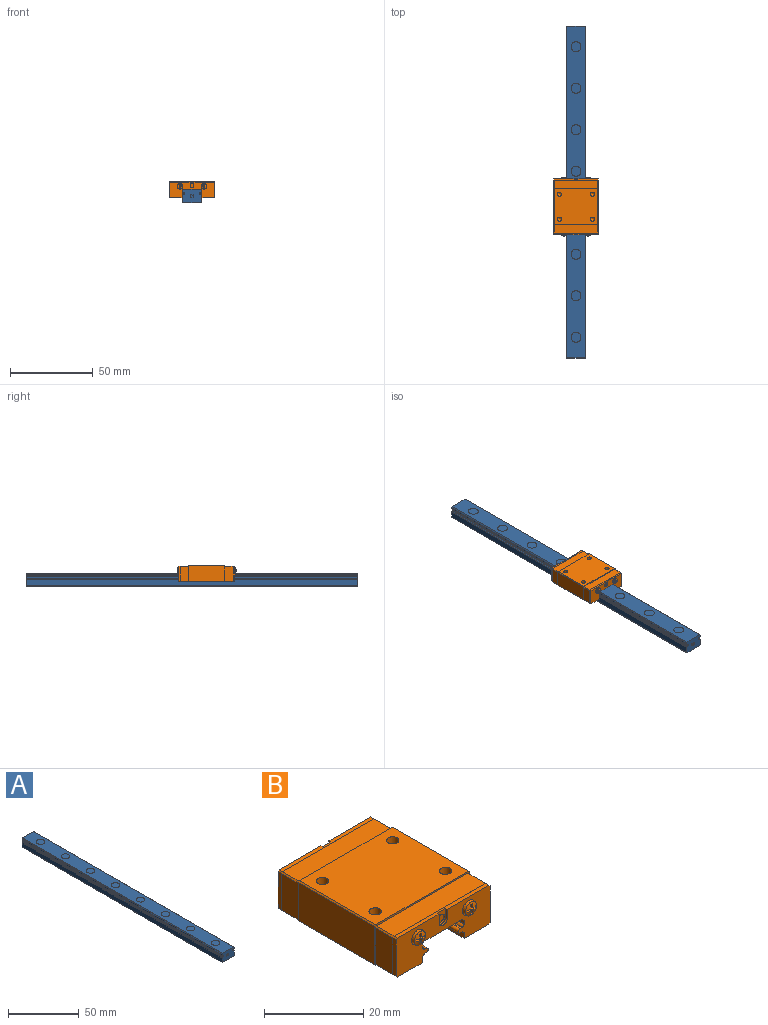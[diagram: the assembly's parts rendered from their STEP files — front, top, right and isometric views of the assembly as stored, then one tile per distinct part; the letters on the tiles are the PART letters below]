
ASSEMBLY  parts=2 mates=1
PART A: 141 faces, bbox 12x200x8 mm
  f0: cylinder r=0.5mm len=200mm, axis (0,1,0), area 377.3mm2, adj f82,f106,f134,f135
  f1: cylinder r=0.5mm len=200mm, axis (0,1,0), area 377.3mm2, adj f82,f106,f121,f122
  f2: cylinder r=1.75mm len=3.5mm, axis (0,0,-1), area 38.5mm2, adj f114,f115
  f3: cylinder r=3mm len=6mm, axis (0,0,-1), area 0.2mm2, adj f40,f128
  f4: cylinder r=1.75mm len=3.5mm, axis (0,0,-1), area 38.5mm2, adj f113,f115
  f5: cylinder r=3mm len=6mm, axis (0,0,-1), area 0.2mm2, adj f38,f128
  f6: cylinder r=1.75mm len=3.5mm, axis (0,0,-1), area 38.5mm2, adj f112,f115
  f7: cylinder r=3mm len=6mm, axis (0,0,-1), area 0.2mm2, adj f36,f128
  f8: cylinder r=1.75mm len=3.5mm, axis (0,0,-1), area 38.5mm2, adj f111,f115
  f9: cylinder r=3mm len=6mm, axis (0,0,-1), area 0.2mm2, adj f34,f128
  f10: cylinder r=1.75mm len=3.5mm, axis (0,0,-1), area 38.5mm2, adj f110,f115
  f11: cylinder r=3mm len=6mm, axis (0,0,-1), area 0.2mm2, adj f32,f128
  f12: cylinder r=1.75mm len=3.5mm, axis (0,0,-1), area 38.5mm2, adj f109,f115
  f13: cylinder r=3mm len=6mm, axis (0,0,-1), area 0.2mm2, adj f30,f128
  f14: cylinder r=1.75mm len=3.5mm, axis (0,0,-1), area 38.5mm2, adj f108,f115
  f15: cylinder r=3mm len=6mm, axis (0,0,-1), area 0.2mm2, adj f28,f128
  f16: cylinder r=1.75mm len=3.5mm, axis (0,0,-1), area 38.5mm2, adj f107,f115
  f17: cylinder r=3mm len=6mm, axis (0,0,-1), area 0.2mm2, adj f26,f128
  f18: cylinder r=3mm len=6mm, axis (0,0,-1), area 75.2mm2, adj f41,f114
  f19: cylinder r=3mm len=6mm, axis (0,0,-1), area 75.2mm2, adj f39,f113
  f20: cylinder r=3mm len=6mm, axis (0,0,-1), area 75.2mm2, adj f37,f112
  f21: cylinder r=3mm len=6mm, axis (0,0,-1), area 75.2mm2, adj f35,f111
  f22: cylinder r=3mm len=6mm, axis (0,0,-1), area 75.2mm2, adj f33,f110
  f23: cylinder r=3mm len=6mm, axis (0,0,-1), area 75.2mm2, adj f31,f109
  f24: cylinder r=3mm len=6mm, axis (0,0,-1), area 75.2mm2, adj f29,f108
  f25: cylinder r=3mm len=6mm, axis (0,0,-1), area 75.2mm2, adj f27,f107
  f26: plane 6x6mm, normal (0,0,1), area 28.3mm2, adj f17
  f27: plane 6x6mm, normal (0,0,-1), area 28.3mm2, adj f25
  f28: plane 6x6mm, normal (0,0,1), area 28.3mm2, adj f15
  f29: plane 6x6mm, normal (0,0,-1), area 28.3mm2, adj f24
  f30: plane 6x6mm, normal (0,0,1), area 28.3mm2, adj f13
  f31: plane 6x6mm, normal (0,0,-1), area 28.3mm2, adj f23
  f32: plane 6x6mm, normal (0,0,1), area 28.3mm2, adj f11
  f33: plane 6x6mm, normal (0,0,-1), area 28.3mm2, adj f22
  f34: plane 6x6mm, normal (0,0,1), area 28.3mm2, adj f9
  f35: plane 6x6mm, normal (0,0,-1), area 28.3mm2, adj f21
  f36: plane 6x6mm, normal (0,0,1), area 28.3mm2, adj f7
  f37: plane 6x6mm, normal (0,0,-1), area 28.3mm2, adj f20
  f38: plane 6x6mm, normal (0,0,1), area 28.3mm2, adj f5
  f39: plane 6x6mm, normal (0,0,-1), area 28.3mm2, adj f19
  f40: plane 6x6mm, normal (0,0,1), area 28.3mm2, adj f3
  f41: plane 6x6mm, normal (0,0,-1), area 28.3mm2, adj f18
  f42: plane 0.63x0mm, normal (1,0,0), area 0mm2, adj f43,f49,f54,f82
  f43: plane 0.44x0mm, normal (0,0,-1), area 0mm2, adj f42,f44,f54,f82
  f44: plane 0.1x0mm, normal (1,0,0), area 0mm2, adj f43,f45,f54,f82
  f45: plane 0.44x0mm, normal (0,0,1), area 0mm2, adj f44,f46,f54,f82
  f46: plane 0.63x0mm, normal (1,0,0), area 0mm2, adj f45,f47,f54,f82
  f47: plane 0.81x0mm, normal (0,0,-1), area 0mm2, adj f46,f48,f54,f82
  f48: plane 0.1x0mm, normal (1,0,0), area 0mm2, adj f47,f53,f54,f82
  f49: plane 0.81x0mm, normal (0,0,1), area 0mm2, adj f42,f50,f54,f82
  f50: plane 0.1x0mm, normal (1,0,0), area 0mm2, adj f49,f51,f54,f82
  f51: plane 0.91x0mm, normal (0,0,-1), area 0mm2, adj f50,f52,f54,f82
  f52: plane 1.57x0mm, normal (-1,0,0), area 0mm2, adj f51,f53,f54,f82
  f53: plane 0.91x0mm, normal (0,0,1), area 0mm2, adj f48,f52,f54,f82
  f54: plane 1.57x0.91mm, normal (0,1,0), area 0.4mm2, adj f42,f43,f44,f45,f46,f47,f48,f49
  f55: plane 0.09x0mm, normal (-1,0,0), area 0mm2, adj f56,f69,f81,f82
  f56: plane 0.15x0.07mm, normal (-0.9,0,-0.44), area 0mm2, adj f55,f57,f81,f82
  f57: plane 0.08x0.08mm, normal (-0.7,0,-0.71), area 0mm2, adj f56,f58,f81,f82
  f58: plane 0.15x0.07mm, normal (-0.44,0,-0.9), area 0mm2, adj f57,f59,f81,f82
  f59: plane 0.3x0mm, normal (0,0,-1), area 0mm2, adj f58,f60,f81,f82
  f60: plane 0.15x0.08mm, normal (0.45,0,-0.9), area 0mm2, adj f59,f61,f81,f82
  f61: plane 0.08x0.08mm, normal (0.7,0,-0.71), area 0mm2, adj f60,f62,f81,f82
  f62: plane 0.15x0.08mm, normal (0.9,0,-0.44), area 0mm2, adj f61,f63,f81,f82
  f63: plane 0.16x0mm, normal (1,0,0), area 0mm2, adj f62,f64,f81,f82
  f64: plane 0.15x0.08mm, normal (0.89,0,0.45), area 0mm2, adj f63,f65,f81,f82
  f65: plane 0.3x0.22mm, normal (0.8,0,0.6), area 0mm2, adj f64,f66,f81,f82
  f66: plane 0.56x0.49mm, normal (0.75,0,0.66), area 0mm2, adj f65,f67,f81,f82
  f67: plane 0.86x0mm, normal (0,0,-1), area 0mm2, adj f66,f68,f81,f82
  f68: plane 0.1x0mm, normal (1,0,0), area 0mm2, adj f67,f80,f81,f82
  f69: plane 0.11x0mm, normal (0,0,1), area 0mm2, adj f55,f70,f81,f82
  f70: plane 0.09x0mm, normal (1,0,0), area 0mm2, adj f69,f71,f81,f82
  f71: plane 0.14x0.07mm, normal (0.89,0,0.45), area 0mm2, adj f70,f72,f81,f82
  f72: plane 0.14x0.07mm, normal (0.45,0,0.89), area 0mm2, adj f71,f73,f81,f82
  f73: plane 0.28x0mm, normal (0,0,1), area 0mm2, adj f72,f74,f81,f82
  f74: plane 0.14x0.07mm, normal (-0.45,0,0.89), area 0mm2, adj f73,f75,f81,f82
  f75: plane 0.14x0.07mm, normal (-0.9,0,0.44), area 0mm2, adj f74,f76,f81,f82
  f76: plane 0.14x0mm, normal (-1,0,0), area 0mm2, adj f75,f77,f81,f82
  f77: plane 0.14x0.07mm, normal (-0.9,0,-0.44), area 0mm2, adj f76,f78,f81,f82
  f78: plane 0.29x0.22mm, normal (-0.8,0,-0.6), area 0mm2, adj f77,f79,f81,f82
  f79: plane 0.69x0.61mm, normal (-0.75,0,-0.66), area 0mm2, adj f78,f80,f81,f82
  f80: plane 1.08x0mm, normal (0,0,1), area 0mm2, adj f68,f79,f81,f82
  f81: plane 1.57x1.08mm, normal (0,1,0), area 0.4mm2, adj f55,f56,f57,f58,f59,f60,f61,f62
  f82: plane 12x8mm, normal (0,1,0), area 90.8mm2, adj f0,f1,f42,f43,f44,f45,f46,f47
  f83: plane 0.63x0mm, normal (-1,0,0), area 0mm2, adj f84,f90,f95,f106
  f84: plane 0.44x0mm, normal (0,0,-1), area 0mm2, adj f83,f85,f95,f106
  f85: plane 0.1x0mm, normal (-1,0,0), area 0mm2, adj f84,f86,f95,f106
  f86: plane 0.44x0mm, normal (0,0,1), area 0mm2, adj f85,f87,f95,f106
  f87: plane 0.63x0mm, normal (-1,0,0), area 0mm2, adj f86,f88,f95,f106
  f88: plane 0.81x0mm, normal (0,0,-1), area 0mm2, adj f87,f89,f95,f106
  f89: plane 0.1x0mm, normal (-1,0,0), area 0mm2, adj f88,f94,f95,f106
  f90: plane 0.81x0mm, normal (0,0,1), area 0mm2, adj f83,f91,f95,f106
  f91: plane 0.1x0mm, normal (-1,0,0), area 0mm2, adj f90,f92,f95,f106
  f92: plane 0.91x0mm, normal (0,0,-1), area 0mm2, adj f91,f93,f95,f106
  f93: plane 1.57x0mm, normal (1,0,0), area 0mm2, adj f92,f94,f95,f106
  f94: plane 0.91x0mm, normal (0,0,1), area 0mm2, adj f89,f93,f95,f106
  f95: plane 1.57x0.91mm, normal (0,-1,0), area 0.4mm2, adj f83,f84,f85,f86,f87,f88,f89,f90
  f96: plane 0.11x0mm, normal (1,0,0), area 0mm2, adj f97,f101,f105,f106
  f97: plane 0.15x0.08mm, normal (0.45,0,-0.89), area 0mm2, adj f96,f98,f105,f106
  f98: plane 0.22x0.22mm, normal (0.71,0,-0.71), area 0mm2, adj f97,f99,f105,f106
  f99: plane 0.02x0mm, normal (0,0,-1), area 0mm2, adj f98,f100,f105,f106
  f100: plane 1.57x0mm, normal (-1,0,0), area 0mm2, adj f99,f104,f105,f106
  f101: plane 0.17x0.09mm, normal (-0.44,0,0.9), area 0mm2, adj f96,f102,f105,f106
  f102: plane 0.12x0.12mm, normal (-0.71,0,0.7), area 0mm2, adj f101,f103,f105,f106
  f103: plane 1.37x0mm, normal (1,0,0), area 0mm2, adj f102,f104,f105,f106
  f104: plane 0.1x0mm, normal (0,0,1), area 0mm2, adj f100,f103,f105,f106
  f105: plane 1.57x0.4mm, normal (0,-1,0), area 0.2mm2, adj f96,f97,f98,f99,f100,f101,f102,f103
  f106: plane 12x8mm, normal (0,-1,0), area 90.9mm2, adj f0,f1,f83,f84,f85,f86,f87,f88
  f107: plane 6x6mm, normal (0,0,1), area 18.7mm2, adj f16,f25
  f108: plane 6x6mm, normal (0,0,1), area 18.7mm2, adj f14,f24
  f109: plane 6x6mm, normal (0,0,1), area 18.7mm2, adj f12,f23
  f110: plane 6x6mm, normal (0,0,1), area 18.7mm2, adj f10,f22
  f111: plane 6x6mm, normal (0,0,1), area 18.7mm2, adj f8,f21
  f112: plane 6x6mm, normal (0,0,1), area 18.7mm2, adj f6,f20
  f113: plane 6x6mm, normal (0,0,1), area 18.7mm2, adj f4,f19
  f114: plane 6x6mm, normal (0,0,1), area 18.7mm2, adj f2,f18
  f115: plane 200x11mm, normal (0,0,-1), area 2123mm2, adj f2,f4,f6,f8,f10,f12,f14,f16
  f116: plane 200x0.5mm, normal (-0.71,0,-0.71), area 141.4mm2, adj f82,f106,f115,f117
  f117: plane 200x3.82mm, normal (-1,0,0), area 764.3mm2, adj f82,f106,f116,f118
  f118: cylinder r=0.16mm len=200mm, axis (0,1,0), area 33.9mm2, adj f82,f106,f117,f119
  f119: cylinder r=1.14mm len=200mm, axis (0,1,0), area 125.3mm2, adj f82,f106,f118,f120
  f120: cylinder r=0.16mm len=200mm, axis (0,1,0), area 33.9mm2, adj f82,f106,f119,f121
  f121: plane 200x0.42mm, normal (0,0,1), area 84.3mm2, adj f1,f82,f106,f120
  f122: plane 200x0.42mm, normal (0,0,-1), area 84.3mm2, adj f1,f82,f106,f123
  f123: cylinder r=0.16mm len=200mm, axis (0,1,0), area 33.9mm2, adj f82,f106,f122,f124
  f124: cylinder r=1.14mm len=200mm, axis (0,1,0), area 125.3mm2, adj f82,f106,f123,f125
  f125: cylinder r=0.16mm len=200mm, axis (0,1,0), area 33.9mm2, adj f82,f106,f124,f126
  f126: plane 200x0.82mm, normal (-1,0,0), area 164.3mm2, adj f82,f106,f125,f127
  f127: plane 200x0.59mm, normal (-0.76,0,0.65), area 154.4mm2, adj f82,f106,f126,f128
  f128: plane 200x11mm, normal (0,0,1), area 1973.8mm2, adj f3,f5,f7,f9,f11,f13,f15,f17
  f129: plane 200x0.59mm, normal (0.76,0,0.65), area 154.4mm2, adj f82,f106,f128,f130
  f130: plane 200x0.82mm, normal (1,0,0), area 164.3mm2, adj f82,f106,f129,f131
  f131: cylinder r=0.16mm len=200mm, axis (0,1,0), area 33.9mm2, adj f82,f106,f130,f132
  f132: cylinder r=1.14mm len=200mm, axis (0,1,0), area 125.3mm2, adj f82,f106,f131,f133
  f133: cylinder r=0.16mm len=200mm, axis (0,1,0), area 33.9mm2, adj f82,f106,f132,f134
  f134: plane 200x0.42mm, normal (0,0,-1), area 84.3mm2, adj f0,f82,f106,f133
  f135: plane 200x0.42mm, normal (0,0,1), area 84.3mm2, adj f0,f82,f106,f136
  f136: cylinder r=0.16mm len=200mm, axis (0,1,0), area 33.9mm2, adj f82,f106,f135,f137
  f137: cylinder r=1.14mm len=200mm, axis (0,1,0), area 125.3mm2, adj f82,f106,f136,f138
  f138: cylinder r=0.16mm len=200mm, axis (0,1,0), area 33.9mm2, adj f82,f106,f137,f139
  f139: plane 200x3.82mm, normal (1,0,0), area 764.3mm2, adj f82,f106,f138,f140
  f140: plane 200x0.5mm, normal (0.71,0,-0.71), area 141.4mm2, adj f82,f106,f115,f139
PART B: 172 faces, bbox 27x35.9x10 mm
  f0: cylinder r=1.25mm len=3.5mm, axis (0,0,-1), area 27.5mm2, adj f1,f158
  f1: cone r=0.62mm half-angle=59deg, axis (0,0,1), area 5.7mm2, adj f0
  f2: cylinder r=1.25mm len=3.5mm, axis (0,0,-1), area 27.5mm2, adj f3,f158
  f3: cone r=0.62mm half-angle=59deg, axis (0,0,1), area 5.7mm2, adj f2
  f4: cylinder r=1.25mm len=3.5mm, axis (0,0,-1), area 27.5mm2, adj f5,f158
  f5: cone r=0.62mm half-angle=59deg, axis (0,0,1), area 5.7mm2, adj f4
  f6: cylinder r=1.25mm len=3.5mm, axis (0,0,-1), area 27.5mm2, adj f7,f158
  f7: cone r=0.62mm half-angle=59deg, axis (0,0,1), area 5.7mm2, adj f6
  f8: cylinder r=0.5mm len=33.7mm, axis (0,1,0), area 63.6mm2, adj f58,f115,f148,f149
  f9: cylinder r=0.5mm len=33.7mm, axis (0,1,0), area 63.6mm2, adj f58,f115,f137,f138
  f10: cylinder r=1.15mm len=2.3mm, axis (0,1,0), area 3.6mm2, adj f114,f124
  f11: cylinder r=1.75mm len=3.5mm, axis (0,1,0), area 5.5mm2, adj f109,f115
  f12: cylinder r=1.75mm len=3.5mm, axis (0,1,0), area 5.5mm2, adj f108,f115
  f13: cone r=0.85mm half-angle=5deg, axis (0,1,0), area 11.5mm2, adj f14,f109
  f14: cone r=0.8mm half-angle=72.7deg, axis (0,1,0), area 6.3mm2, adj f13,f96,f97,f98,f99,f100,f101,f102
  f15: cone r=0.85mm half-angle=5deg, axis (0,1,0), area 11.5mm2, adj f16,f108
  f16: cone r=0.8mm half-angle=72.7deg, axis (0,1,0), area 6.3mm2, adj f15,f83,f84,f85,f86,f87,f88,f89
  f17: cylinder r=1.15mm len=2.3mm, axis (0,-1,0), area 3.6mm2, adj f57,f67
  f18: cylinder r=1.75mm len=3.5mm, axis (0,-1,0), area 5.5mm2, adj f52,f58
  f19: cylinder r=1.75mm len=3.5mm, axis (0,-1,0), area 5.5mm2, adj f51,f58
  f20: cone r=0.85mm half-angle=5deg, axis (0,-1,0), area 11.5mm2, adj f21,f52
  f21: cone r=0.8mm half-angle=72.7deg, axis (0,-1,0), area 6.3mm2, adj f20,f39,f40,f41,f42,f43,f44,f45
  f22: cone r=0.85mm half-angle=5deg, axis (0,-1,0), area 11.5mm2, adj f23,f51
  f23: cone r=0.8mm half-angle=72.7deg, axis (0,-1,0), area 6.3mm2, adj f22,f26,f27,f28,f29,f30,f31,f32
  f24: plane 26.6x9.6mm, normal (0,-1,0), area 0.3mm2, adj f55,f59,f60,f61,f62,f63,f64,f65
  f25: plane 2.4x2.4mm, normal (0,1,0), area 2.1mm2, adj f26,f27,f28,f29,f30,f31,f32,f33
  f26: plane 0.93x0.49mm, normal (0,0,1), area 0.4mm2, adj f23,f25,f29,f31
  f27: plane 0.93x0.49mm, normal (0,0,-1), area 0.4mm2, adj f23,f25,f28,f30
  f28: plane 1.36x1.29mm, normal (-1,0,0), area 1mm2, adj f23,f25,f27,f36
  f29: plane 1.36x1.29mm, normal (-1,0,0), area 1mm2, adj f23,f25,f26,f32
  f30: plane 1.36x1.29mm, normal (1,0,0), area 1mm2, adj f23,f25,f27,f33
  f31: plane 1.36x1.29mm, normal (1,0,0), area 1mm2, adj f23,f25,f26,f34
  f32: plane 1.36x1.29mm, normal (0,0,1), area 1mm2, adj f23,f25,f29,f35
  f33: plane 1.36x1.29mm, normal (0,0,-1), area 1mm2, adj f23,f25,f30,f37
  f34: plane 1.36x1.29mm, normal (0,0,1), area 1mm2, adj f23,f25,f31,f37
  f35: plane 0.93x0.49mm, normal (-1,0,0), area 0.4mm2, adj f23,f25,f32,f36
  f36: plane 1.36x1.29mm, normal (0,0,-1), area 1mm2, adj f23,f25,f28,f35
  f37: plane 0.94x0.49mm, normal (1,0,0), area 0.4mm2, adj f23,f25,f33,f34
  f38: plane 2.4x2.4mm, normal (0,1,0), area 2.1mm2, adj f39,f40,f41,f42,f43,f44,f45,f46
  f39: plane 0.93x0.49mm, normal (0,0,1), area 0.4mm2, adj f21,f38,f42,f44
  f40: plane 0.93x0.49mm, normal (0,0,-1), area 0.4mm2, adj f21,f38,f41,f43
  f41: plane 1.36x1.29mm, normal (-1,0,0), area 1mm2, adj f21,f38,f40,f49
  f42: plane 1.36x1.29mm, normal (-1,0,0), area 1mm2, adj f21,f38,f39,f45
  f43: plane 1.36x1.29mm, normal (1,0,0), area 1mm2, adj f21,f38,f40,f46
  f44: plane 1.36x1.29mm, normal (1,0,0), area 1mm2, adj f21,f38,f39,f47
  f45: plane 1.36x1.29mm, normal (0,0,1), area 1mm2, adj f21,f38,f42,f48
  f46: plane 1.36x1.29mm, normal (0,0,-1), area 1mm2, adj f21,f38,f43,f50
  f47: plane 1.36x1.29mm, normal (0,0,1), area 1mm2, adj f21,f38,f44,f50
  f48: plane 0.93x0.49mm, normal (-1,0,0), area 0.4mm2, adj f21,f38,f45,f49
  f49: plane 1.36x1.29mm, normal (0,0,-1), area 1mm2, adj f21,f38,f41,f48
  f50: plane 0.94x0.49mm, normal (1,0,0), area 0.4mm2, adj f21,f38,f46,f47
  f51: plane 3.5x3.5mm, normal (0,1,0), area 0.5mm2, adj f19,f22
  f52: plane 3.5x3.5mm, normal (0,1,0), area 0.5mm2, adj f18,f20
  f53: plane 2.1x0.5mm, normal (1,0,0), area 1.1mm2, adj f55,f56,f57,f58
  f54: plane 2.1x0.5mm, normal (-1,0,0), area 1.1mm2, adj f55,f56,f57,f58
  f55: plane 26x1mm, normal (0,0,1), area 24.8mm2, adj f24,f53,f54,f57,f58,f62,f63
  f56: cylinder r=1.2mm len=2.4mm, axis (0,-1,0), area 1.9mm2, adj f53,f54,f57,f58
  f57: plane 3.3x2.4mm, normal (0,1,0), area 3.1mm2, adj f17,f53,f54,f55,f56
  f58: plane 26.6x9.6mm, normal (0,1,0), area 172.9mm2, adj f8,f9,f18,f19,f53,f54,f55,f56
  f59: plane 7x1mm, normal (0,0,-1), area 7mm2, adj f24,f58,f65,f134
  f60: plane 7x1mm, normal (0,0,-1), area 7mm2, adj f24,f58,f66,f152
  f61: plane 9x1mm, normal (1,0,0), area 9mm2, adj f24,f58,f62,f66
  f62: plane 1x0.3mm, normal (0.71,0,0.71), area 0.4mm2, adj f24,f55,f58,f61
  f63: plane 1x0.3mm, normal (-0.71,0,0.71), area 0.4mm2, adj f24,f55,f58,f64
  f64: plane 9x1mm, normal (-1,0,0), area 9mm2, adj f24,f58,f63,f65
  f65: plane 1x0.3mm, normal (-0.71,0,-0.71), area 0.4mm2, adj f24,f58,f59,f64
  f66: plane 1x0.3mm, normal (0.71,0,-0.71), area 0.4mm2, adj f24,f58,f60,f61
  f67: plane 2.3x2.3mm, normal (0,1,0), area 4.2mm2, adj f17
  f68: cylinder r=1.14mm len=33.7mm, axis (0,-1,0), area 21.1mm2, adj f58,f115,f150,f151
  f69: cylinder r=1.14mm len=33.7mm, axis (0,-1,0), area 21.1mm2, adj f58,f115,f146,f147
  f70: cylinder r=1.14mm len=33.7mm, axis (0,-1,0), area 21.1mm2, adj f58,f115,f139,f140
  f71: cylinder r=1.14mm len=33.7mm, axis (0,-1,0), area 21.1mm2, adj f58,f115,f135,f136
  f72: plane 7x5mm, normal (0,0,-1), area 35mm2, adj f24,f79,f134,f163
  f73: plane 7x5mm, normal (0,0,-1), area 35mm2, adj f24,f80,f152,f163
  f74: plane 8.99x5mm, normal (1,0,0), area 45mm2, adj f24,f75,f80,f163
  f75: plane 5x0.3mm, normal (0.71,0,0.71), area 2.1mm2, adj f24,f74,f76,f163
  f76: plane 25.99x5mm, normal (0,0,1), area 130mm2, adj f24,f75,f77,f163
  f77: plane 5x0.3mm, normal (-0.71,0,0.71), area 2.1mm2, adj f24,f76,f78,f163
  f78: plane 8.99x5mm, normal (-1,0,0), area 45mm2, adj f24,f77,f79,f163
  f79: plane 5x0.3mm, normal (-0.71,0,-0.71), area 2.1mm2, adj f24,f72,f78,f163
  f80: plane 5x0.3mm, normal (0.71,0,-0.71), area 2.1mm2, adj f24,f73,f74,f163
  f81: plane 26.6x9.6mm, normal (0,1,0), area 0.3mm2, adj f112,f116,f117,f118,f119,f120,f121,f122
  f82: plane 2.4x2.4mm, normal (0,-1,0), area 2.1mm2, adj f83,f84,f85,f86,f87,f88,f89,f90
  f83: plane 0.93x0.49mm, normal (0,0,1), area 0.4mm2, adj f16,f82,f86,f88
  f84: plane 0.93x0.49mm, normal (0,0,-1), area 0.4mm2, adj f16,f82,f85,f87
  f85: plane 1.36x1.29mm, normal (1,0,0), area 1mm2, adj f16,f82,f84,f93
  f86: plane 1.36x1.29mm, normal (1,0,0), area 1mm2, adj f16,f82,f83,f89
  f87: plane 1.36x1.29mm, normal (-1,0,0), area 1mm2, adj f16,f82,f84,f90
  f88: plane 1.36x1.29mm, normal (-1,0,0), area 1mm2, adj f16,f82,f83,f91
  f89: plane 1.36x1.29mm, normal (0,0,1), area 1mm2, adj f16,f82,f86,f92
  f90: plane 1.36x1.29mm, normal (0,0,-1), area 1mm2, adj f16,f82,f87,f94
  f91: plane 1.36x1.29mm, normal (0,0,1), area 1mm2, adj f16,f82,f88,f94
  f92: plane 0.93x0.49mm, normal (1,0,0), area 0.4mm2, adj f16,f82,f89,f93
  f93: plane 1.36x1.29mm, normal (0,0,-1), area 1mm2, adj f16,f82,f85,f92
  f94: plane 0.94x0.49mm, normal (-1,0,0), area 0.4mm2, adj f16,f82,f90,f91
  f95: plane 2.4x2.4mm, normal (0,-1,0), area 2.1mm2, adj f96,f97,f98,f99,f100,f101,f102,f103
  f96: plane 0.93x0.49mm, normal (0,0,1), area 0.4mm2, adj f14,f95,f99,f101
  f97: plane 0.93x0.49mm, normal (0,0,-1), area 0.4mm2, adj f14,f95,f98,f100
  f98: plane 1.36x1.29mm, normal (1,0,0), area 1mm2, adj f14,f95,f97,f106
  f99: plane 1.36x1.29mm, normal (1,0,0), area 1mm2, adj f14,f95,f96,f102
  f100: plane 1.36x1.29mm, normal (-1,0,0), area 1mm2, adj f14,f95,f97,f103
  f101: plane 1.36x1.29mm, normal (-1,0,0), area 1mm2, adj f14,f95,f96,f104
  f102: plane 1.36x1.29mm, normal (0,0,1), area 1mm2, adj f14,f95,f99,f105
  f103: plane 1.36x1.29mm, normal (0,0,-1), area 1mm2, adj f14,f95,f100,f107
  f104: plane 1.36x1.29mm, normal (0,0,1), area 1mm2, adj f14,f95,f101,f107
  f105: plane 0.93x0.49mm, normal (1,0,0), area 0.4mm2, adj f14,f95,f102,f106
  f106: plane 1.36x1.29mm, normal (0,0,-1), area 1mm2, adj f14,f95,f98,f105
  f107: plane 0.94x0.49mm, normal (-1,0,0), area 0.4mm2, adj f14,f95,f103,f104
  f108: plane 3.5x3.5mm, normal (0,-1,0), area 0.5mm2, adj f12,f15
  f109: plane 3.5x3.5mm, normal (0,-1,0), area 0.5mm2, adj f11,f13
  f110: plane 2.1x0.5mm, normal (-1,0,0), area 1mm2, adj f112,f113,f114,f115
  f111: plane 2.1x0.5mm, normal (1,0,0), area 1mm2, adj f112,f113,f114,f115
  f112: plane 26x1mm, normal (0,0,1), area 24.8mm2, adj f81,f110,f111,f114,f115,f119,f120
  f113: cylinder r=1.2mm len=2.4mm, axis (0,1,0), area 1.9mm2, adj f110,f111,f114,f115
  f114: plane 3.3x2.4mm, normal (0,-1,0), area 3.1mm2, adj f10,f110,f111,f112,f113
  f115: plane 26.6x9.6mm, normal (0,-1,0), area 172.9mm2, adj f8,f9,f11,f12,f68,f69,f70,f71
  f116: plane 7x1mm, normal (0,0,-1), area 7mm2, adj f81,f115,f122,f152
  f117: plane 7x1mm, normal (0,0,-1), area 7mm2, adj f81,f115,f123,f134
  f118: plane 9x1mm, normal (-1,0,0), area 9mm2, adj f81,f115,f119,f123
  f119: plane 1x0.3mm, normal (-0.71,0,0.71), area 0.4mm2, adj f81,f112,f115,f118
  f120: plane 1x0.3mm, normal (0.71,0,0.71), area 0.4mm2, adj f81,f112,f115,f121
  f121: plane 9x1mm, normal (1,0,0), area 9mm2, adj f81,f115,f120,f122
  f122: plane 1x0.3mm, normal (0.71,0,-0.71), area 0.4mm2, adj f81,f115,f116,f121
  f123: plane 1x0.3mm, normal (-0.71,0,-0.71), area 0.4mm2, adj f81,f115,f117,f118
  f124: plane 2.3x2.3mm, normal (0,-1,0), area 4.2mm2, adj f10
  f125: plane 7x5mm, normal (0,0,-1), area 35mm2, adj f81,f132,f152,f153
  f126: plane 7x5mm, normal (0,0,-1), area 35mm2, adj f81,f133,f134,f153
  f127: plane 8.99x5mm, normal (-1,0,0), area 44.9mm2, adj f81,f128,f133,f153
  f128: plane 5x0.3mm, normal (-0.71,0,0.71), area 2.1mm2, adj f81,f127,f129,f153
  f129: plane 25.99x5mm, normal (0,0,1), area 129.9mm2, adj f81,f128,f130,f153
  f130: plane 5x0.3mm, normal (0.71,0,0.71), area 2.1mm2, adj f81,f129,f131,f153
  f131: plane 8.99x5mm, normal (1,0,0), area 45mm2, adj f81,f130,f132,f153
  f132: plane 5x0.3mm, normal (0.71,0,-0.71), area 2.1mm2, adj f81,f125,f131,f153
  f133: plane 5x0.3mm, normal (-0.71,0,-0.71), area 2.1mm2, adj f81,f126,f127,f153
  f134: plane 33.7x1.32mm, normal (1,0,0), area 44.5mm2, adj f24,f58,f59,f72,f81,f115,f117,f126
  f135: cylinder r=0.16mm len=33.7mm, axis (0,1,0), area 5.7mm2, adj f58,f71,f115,f134
  f136: cylinder r=0.16mm len=33.7mm, axis (0,1,0), area 5.7mm2, adj f58,f71,f115,f137
  f137: plane 33.7x0.42mm, normal (0,0,-1), area 14.2mm2, adj f9,f58,f115,f136
  f138: plane 33.7x0.42mm, normal (0,0,1), area 14.2mm2, adj f9,f58,f115,f139
  f139: cylinder r=0.16mm len=33.7mm, axis (0,1,0), area 5.7mm2, adj f58,f70,f115,f138
  f140: cylinder r=0.16mm len=33.7mm, axis (0,1,0), area 5.7mm2, adj f58,f70,f115,f141
  f141: plane 33.7x0.82mm, normal (1,0,0), area 27.7mm2, adj f58,f115,f140,f142
  f142: plane 33.7x0.59mm, normal (0.76,0,-0.65), area 26mm2, adj f58,f115,f141,f143
  f143: plane 33.7x11mm, normal (0,0,-1), area 370.7mm2, adj f58,f115,f142,f144
  f144: plane 33.7x0.59mm, normal (-0.76,0,-0.65), area 26mm2, adj f58,f115,f143,f145
  f145: plane 33.7x0.82mm, normal (-1,0,0), area 27.7mm2, adj f58,f115,f144,f146
  f146: cylinder r=0.16mm len=33.7mm, axis (0,1,0), area 5.7mm2, adj f58,f69,f115,f145
  f147: cylinder r=0.16mm len=33.7mm, axis (0,1,0), area 5.7mm2, adj f58,f69,f115,f148
  f148: plane 33.7x0.42mm, normal (0,0,1), area 14.2mm2, adj f8,f58,f115,f147
  f149: plane 33.7x0.42mm, normal (0,0,-1), area 14.2mm2, adj f8,f58,f115,f150
  f150: cylinder r=0.16mm len=33.7mm, axis (0,1,0), area 5.7mm2, adj f58,f68,f115,f149
  f151: cylinder r=0.16mm len=33.7mm, axis (0,1,0), area 5.7mm2, adj f58,f68,f115,f152
  f152: plane 33.7x1.32mm, normal (-1,0,0), area 44.5mm2, adj f24,f58,f60,f73,f81,f115,f116,f125
  f153: plane 27x10mm, normal (0,-1,0), area 14.9mm2, adj f125,f126,f127,f128,f129,f130,f131,f132
  f154: plane 21.7x7.2mm, normal (0,0,-1), area 156.2mm2, adj f152,f153,f161,f163
  f155: plane 21.7x7.2mm, normal (0,0,-1), area 156.2mm2, adj f134,f153,f162,f163
  f156: plane 21.7x9.4mm, normal (-1,0,0), area 204mm2, adj f153,f157,f162,f163
  f157: plane 21.7x0.3mm, normal (-0.71,0,0.71), area 9.2mm2, adj f153,f156,f158,f163
  f158: plane 26.4x21.7mm, normal (0,0,1), area 553.2mm2, adj f0,f2,f4,f6,f153,f157,f159,f163
  f159: plane 21.7x0.3mm, normal (0.71,0,0.71), area 9.2mm2, adj f153,f158,f160,f163
  f160: plane 21.7x9.4mm, normal (1,0,0), area 204mm2, adj f153,f159,f161,f163
  f161: plane 21.7x0.3mm, normal (0.71,0,-0.71), area 9.2mm2, adj f153,f154,f160,f163
  f162: plane 21.7x0.3mm, normal (-0.71,0,-0.71), area 9.2mm2, adj f153,f155,f156,f163
  f163: plane 27x10mm, normal (0,1,0), area 14.9mm2, adj f72,f73,f74,f75,f76,f77,f78,f79
  f164: cone r=0.5mm half-angle=17.1deg, axis (0,-1,0), area 2.7mm2, adj f166,f167
  f165: cylinder r=1.25mm len=2.5mm, axis (0,-1,0), area 3.9mm2, adj f166,f167
  f166: plane 2.5x2.5mm, normal (0,1,0), area 2.3mm2, adj f164,f165
  f167: plane 2.5x2.5mm, normal (0,-1,0), area 3.1mm2, adj f164,f165
  f168: cylinder r=1.25mm len=2.5mm, axis (0,-1,0), area 3.9mm2, adj f170,f171
  f169: cone r=0.5mm half-angle=17.1deg, axis (0,-1,0), area 2.7mm2, adj f170,f171
  f170: plane 2.5x2.5mm, normal (0,-1,0), area 3.1mm2, adj f168,f169
  f171: plane 2.5x2.5mm, normal (0,1,0), area 2.3mm2, adj f168,f169
PLACE A at identity fixed
PLACE B t=(0,74.22,-0.16)mm
MATE slider A.f106 <-> B.f58  axis (0,-1,0) through (0,0,8)mm
